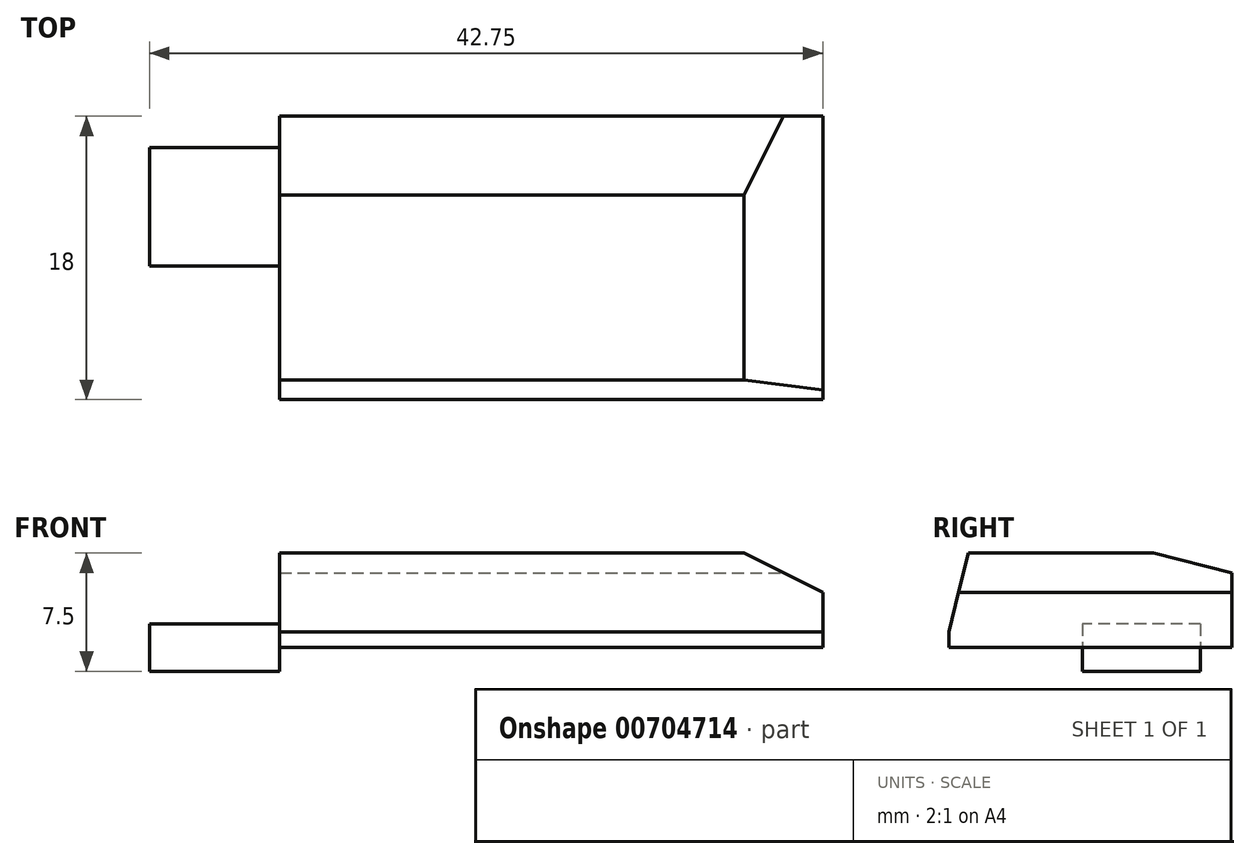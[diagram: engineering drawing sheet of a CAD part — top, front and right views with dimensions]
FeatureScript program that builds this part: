
annotation { "Feature Type Name" : "Feature", "Feature Type Description" : "" }
export const myFeature = defineFeature(function(context is Context, id is Id, definition is map)
    precondition{}
    {
        {
            var Q0;
            Q0=qCreatedBy(makeId("Top.planeOp"),FACE);
            var sketch = newSketch(context, id + "F0", { "sketchPlane" : qUnion([Q0])});
            skLineSegment(sketch, "E0.bottom", {"start": v(-17.25, 9) * mm, "end": v(17.25, 9) * mm});
            skLineSegment(sketch, "E0.top", {"start": v(-17.25, -9) * mm, "end": v(17.25, -9) * mm});
            skLineSegment(sketch, "E0.left", {"start": v(-17.25, 9) * mm, "end": v(-17.25, -9) * mm});
            skLineSegment(sketch, "E0.right", {"start": v(17.25, 9) * mm, "end": v(17.25, -9) * mm});
            skLineSegment(sketch, "E1.bottom", {"start": v(-17.25, 7) * mm, "end": v(-25.5, 7) * mm});
            skLineSegment(sketch, "E1.top", {"start": v(-17.25, -0.5) * mm, "end": v(-25.5, -0.5) * mm});
            skLineSegment(sketch, "E1.left", {"start": v(-17.25, 7) * mm, "end": v(-17.25, -0.5) * mm});
            skLineSegment(sketch, "E1.right", {"start": v(-25.5, 7) * mm, "end": v(-25.5, -0.5) * mm});
            skSolve(sketch);
        }
        {
            var Q0;
            {var subQ4=sQuery(id+"F0.wireOp",EDGE,"E0.bottom");Q0=makeQuery(id+"F0.imprint","IMPRINT",FACE,{"disambiguationData":[TD([[makeQuery(id+"F0.imprint","IMPRINT",EDGE,{"derivedFrom":subQ4}),-1.0]])]});}
            extrude(context, id + "F1", {"entities" : qUnion([Q0]), "depth" : 6 * mm, "offsetDistance" : 25 * mm});
        }
        {
            var Q0;
            {var subQ2=sQuery(id+"F0.wireOp",EDGE,"E1.bottom");Q0=makeQuery(id+"F0.imprint","IMPRINT",FACE,{"disambiguationData":[TD([[makeQuery(id+"F0.imprint","IMPRINT",EDGE,{"derivedFrom":subQ2}),1.0]])]});}
            extrude(context, id + "F2", {"entities" : qUnion([Q0]), "operationType" : NewBodyOperationType.ADD, "depth" : 3 * mm, "offsetDistance" : 25 * mm, "symmetric" : true});
        }
        {
            var Q0;
            Q0=makeQuery(id+"F1.opExtrude","CAP_EDGE",EDGE,{"disambiguationData":[OSD([sQuery(id+"F0.wireOp",EDGE,"E0.top")])],"isStart":false});
            var Q1;
            Q1=makeQuery(id+"F1.opExtrude","CAP_EDGE",EDGE,{"disambiguationData":[OSD([sQuery(id+"F0.wireOp",EDGE,"E0.bottom")])],"isStart":false});
            chamfer(context, id + "F3", {"entities" : qUnion([Q0, Q1]), "chamferType" : ChamferType.TWO_OFFSETS, "width1" : 1.25 * mm, "oppositeDirection" : false, "width2" : 5 * mm, "tangentPropagation" : true});
        }
        {
            var Q0;
            Q0=makeQuery(id+"F1.opExtrude","CAP_EDGE",EDGE,{"disambiguationData":[OSD([sQuery(id+"F0.wireOp",EDGE,"E0.right")])],"isStart":false});
            chamfer(context, id + "F4", {"entities" : qUnion([Q0]), "chamferType" : ChamferType.TWO_OFFSETS, "width1" : 5 * mm, "oppositeDirection" : false, "width2" : 2.5 * mm, "tangentPropagation" : true});
        }
    });
